# Revit family: 201_RON 2-_
name_source: partatom
category: Air Terminals
units: mm (PartAtom-declared; Revit-internal decimal feet)

## family parameters
Always vertical = Yes
Cut with Voids When Loaded = No
Part Type = Normal
Room Calculation Point = Yes
Round Connector Dimension = Use Diameter
Shared = No
Work Plane-Based = No

## types (4) — shared parameters
CAT0 = Yes
CL_Location_5000 = 5000 mm  [stored 16.4042 ft]
CON1 = Yes
CON2 = No
CON3 = No
Description = Wall diffuser with plenum box, rear connection
L_ARR = 400 mm  [stored 1.31234 ft]
Manufacturer = Climecon
QmdConnectorList = 201;D
URL = www.climecon.fi
W_ARR = 400 mm  [stored 1.31234 ft]
XRefLineVPlnId = 7453
YRefLineVPlnId = 7456
magiPartTypeId = 201
magiProductFamilyId = RON 2-*
zero-valued in all types: CLBTZ, H_ARR, MC_Default_elevation

## per-type parameters (varying)
| type | A | A1 | B1 | C1 | C2 | D | F | H1 | L1 | L2 |
| RON 2-100 | 500 mm  [stored 1.64042 ft] | 250 mm  [stored 0.82021 ft] | 89 mm | 24 mm | 49 mm | 100 mm | 125 mm  [stored 0.410105 ft] | 75 mm  [stored 0.246063 ft] | 200 mm  [stored 0.656168 ft] | 160 mm  [stored 0.524934 ft] |
| RON 2-200 | 700 mm  [stored 2.29659 ft] | 350 mm  [stored 1.14829 ft] | 141 mm  [stored 0.462598 ft] | 33 mm | 67 mm | 200 mm | 175 mm  [stored 0.574147 ft] | 125 mm  [stored 0.410105 ft] | 300 mm  [stored 0.984252 ft] | 225 mm  [stored 0.738189 ft] |
| RON 2-160 | 600 mm  [stored 1.9685 ft] | 300 mm  [stored 0.984252 ft] | 113 mm  [stored 0.370735 ft] | 30 mm  [stored 0.0984252 ft] | 60 mm  [stored 0.19685 ft] | 160 mm | 175 mm  [stored 0.574147 ft] | 100 mm  [stored 0.328084 ft] | 250 mm  [stored 0.82021 ft] | 195 mm  [stored 0.639764 ft] |
| RON 2-125 | 600 mm  [stored 1.9685 ft] | 300 mm  [stored 0.984252 ft] | 89 mm | 24 mm | 49 mm | 125 mm | 135 mm  [stored 0.442913 ft] | 75 mm  [stored 0.246063 ft] | 250 mm  [stored 0.82021 ft] | 160 mm  [stored 0.524934 ft] |

note: column(s) folded — value = type name in every type: magiProductCode, magiProductId

note: [stored X ft] marks values corroborated as IEEE doubles in the binary element streams (Revit-internal decimal feet)

## geometry (parser evidence)
native form markers: Sweep x2
no freeform markers — native parametric forms only
